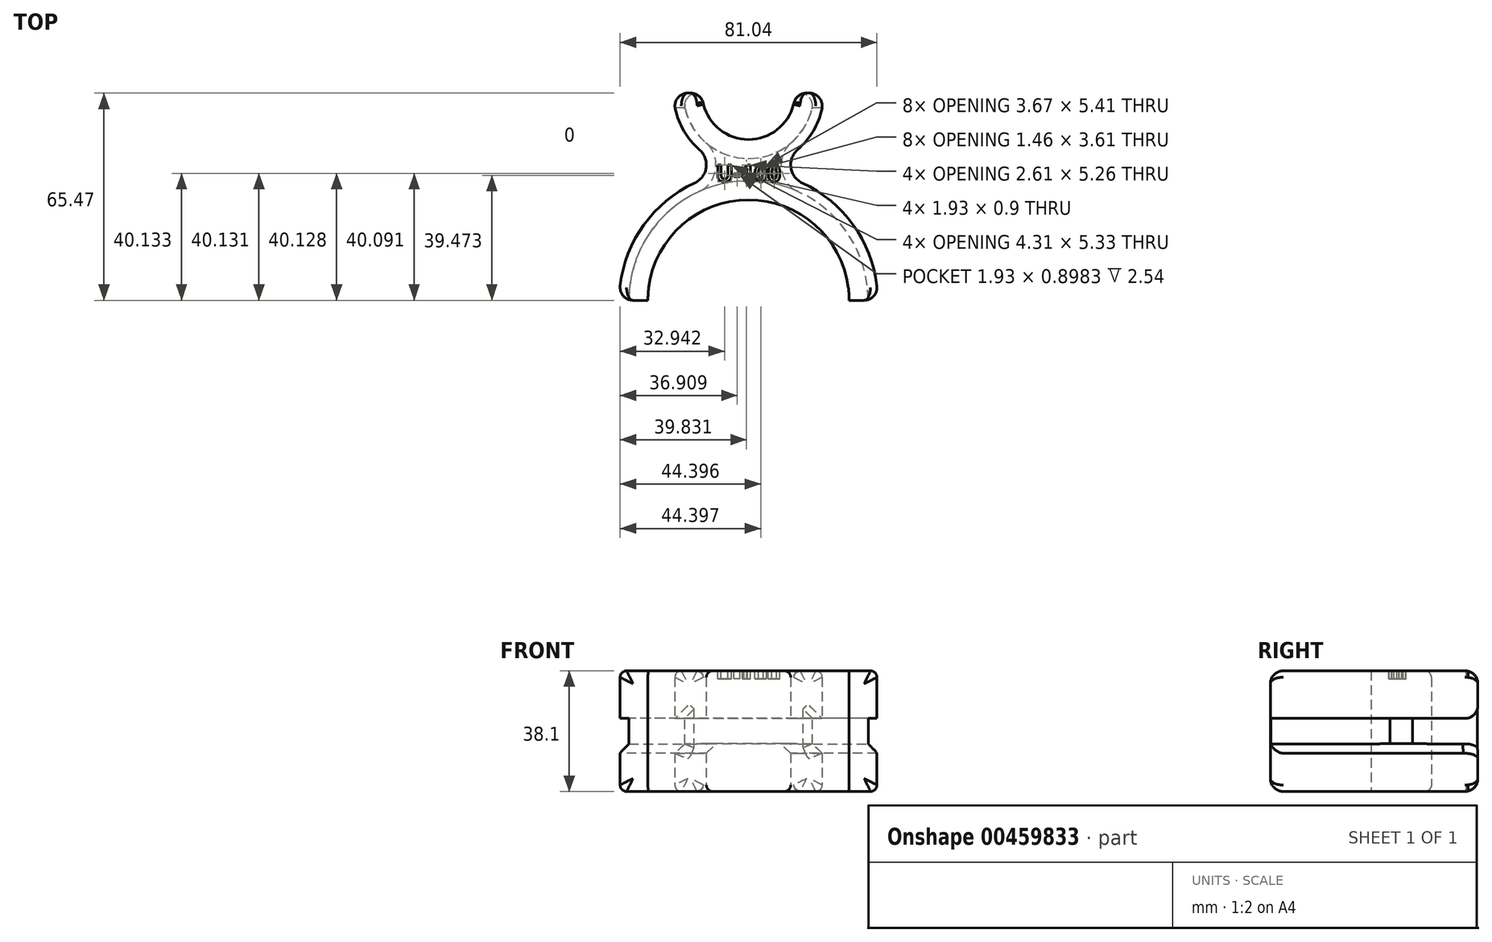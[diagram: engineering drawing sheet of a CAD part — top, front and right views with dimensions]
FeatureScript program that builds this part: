
annotation { "Feature Type Name" : "Feature", "Feature Type Description" : "" }
export const myFeature = defineFeature(function(context is Context, id is Id, definition is map)
    precondition{}
    {
        {
            var Q0;
            Q0=qCreatedBy(makeId("Top.planeOp"),FACE);
            var sketch = newSketch(context, id + "F0", { "sketchPlane" : qUnion([Q0])});
            skArc(sketch, "E0", {"start": v(31.75, -42.8) * mm, "mid": v(0, -11.05) * mm, "end": v(-31.75, -42.8) * mm});
            skLineSegment(sketch, "E1", {"start": v(31.75, -42.8) * mm, "end": v(40.75, -42.8) * mm});
            skArc(sketch, "E2", {"start": v(40.75, -42.8) * mm, "mid": v(34.3, -20.8) * mm, "end": v(17.02, -5.77) * mm});
            skArc(sketch, "E3", {"start": v(15.5, 4.8) * mm, "mid": v(21.53, 12.85) * mm, "end": v(23.66, 22.67) * mm});
            skArc(sketch, "E4", {"start": v(-17.02, -5.77) * mm, "mid": v(-34.3, -20.8) * mm, "end": v(-40.75, -42.8) * mm});
            skArc(sketch, "E5", {"start": v(-23.66, 22.67) * mm, "mid": v(-21.53, 12.85) * mm, "end": v(-15.5, 4.8) * mm});
            skLineSegment(sketch, "E6", {"start": v(-23.66, 22.67) * mm, "end": v(-14.66, 22.67) * mm});
            skLineSegment(sketch, "E7", {"start": v(23.66, 22.67) * mm, "end": v(14.66, 22.67) * mm});
            skLineSegment(sketch, "E8", {"start": v(-40.75, -42.8) * mm, "end": v(-31.75, -42.8) * mm});
            skArc(sketch, "E9", {"start": v(-14.66, 22.67) * mm, "mid": v(0, 8) * mm, "end": v(14.66, 22.67) * mm});
            skArc(sketch, "E10", {"start": v(-17.02, -5.77) * mm, "mid": v(-13.39, -0.9) * mm, "end": v(-15.5, 4.8) * mm});
            skArc(sketch, "E11", {"start": v(15.5, 4.8) * mm, "mid": v(13.39, -0.9) * mm, "end": v(17.02, -5.77) * mm});
            skLineSegment(sketch, "E12", {"start": v(-10.86, 8) * mm, "end": v(15, 8) * mm, "construction": true});
            skLineSegment(sketch, "E13", {"start": v(-10.28, -11.05) * mm, "end": v(13.06, -11.05) * mm, "construction": true});
            skArc(sketch, "E14", {"start": v(-20.66, 22.67) * mm, "mid": v(0, 2) * mm, "end": v(20.66, 22.67) * mm});
            skArc(sketch, "E15", {"start": v(37.75, -42.8) * mm, "mid": v(0, -5.05) * mm, "end": v(-37.75, -42.8) * mm});
            skCircle(sketch, "E16.cCircle", {"center": v(0, 22.67) * mm, "radius": 14.66 * mm, "construction": true});
            skLineSegment(sketch, "E16.0", {"start": v(-14.66, 22.67) * mm, "end": v(-7.33, 35.37) * mm, "construction": true});
            skLineSegment(sketch, "E16.1", {"start": v(-7.33, 35.37) * mm, "end": v(7.33, 35.37) * mm, "construction": true});
            skLineSegment(sketch, "E16.2", {"start": v(7.33, 35.37) * mm, "end": v(14.66, 22.67) * mm, "construction": true});
            skLineSegment(sketch, "E16.3", {"start": v(14.66, 22.67) * mm, "end": v(7.33, 9.97) * mm, "construction": true});
            skLineSegment(sketch, "E16.4", {"start": v(7.33, 9.97) * mm, "end": v(-7.33, 9.97) * mm, "construction": true});
            skLineSegment(sketch, "E16.5", {"start": v(-7.33, 9.97) * mm, "end": v(-14.66, 22.67) * mm, "construction": true});
            skSolve(sketch);
        }
        {
            var Q0;
            {var subQ0=sQuery(id+"F0.wireOp",EDGE,"E9");Q0=makeQuery(id+"F0.imprint","IMPRINT",FACE,{"disambiguationData":[TD([[makeQuery(id+"F0.imprint","IMPRINT",EDGE,{"derivedFrom":subQ0}),-1.0]])]});}
            var Q1;
            {var subQ0=sQuery(id+"F0.wireOp",EDGE,"E0");Q1=makeQuery(id+"F0.imprint","IMPRINT",FACE,{"disambiguationData":[TD([[makeQuery(id+"F0.imprint","IMPRINT",EDGE,{"derivedFrom":subQ0}),-1.0]])]});}
            var Q2;
            {var subQ8=sQuery(id+"F0.wireOp",EDGE,"E2");Q2=makeQuery(id+"F0.imprint","IMPRINT",FACE,{"disambiguationData":[TD([[makeQuery(id+"F0.imprint","IMPRINT",EDGE,{"derivedFrom":subQ8}),1.0]])]});}
            extrude(context, id + "F1", {"entities" : qUnion([Q0, Q1, Q2]), "endBound" : BoundingType.SYMMETRIC, "depth" : 38.1 * mm, "hasSecondDirection" : true, "secondDirectionOppositeDirection" : true, "secondDirectionDepth" : 20 * mm});
        }
        {
            var Q0;
            {var subQ8=sQuery(id+"F0.wireOp",EDGE,"E2");Q0=makeQuery(id+"F0.imprint","IMPRINT",FACE,{"disambiguationData":[TD([[makeQuery(id+"F0.imprint","IMPRINT",EDGE,{"derivedFrom":subQ8}),1.0]])]});}
            extrude(context, id + "F2", {"entities" : qUnion([Q0]), "operationType" : NewBodyOperationType.REMOVE, "endBound" : BoundingType.SYMMETRIC, "oppositeDirection" : true, "depth" : 8 * mm});
        }
        {
            var Q0;
            Q0=makeQuery(id+"F2.boolean.opBoolean","COPY",EDGE,{"derivedFrom":makeQuery(id+"F2.opExtrude","CAP_EDGE",EDGE,{"disambiguationData":[OSD([sQuery(id+"F0.wireOp",EDGE,"E2")])],"isStart":true})});
            var Q1;
            Q1=makeQuery(id+"F2.boolean.opBoolean","COPY",EDGE,{"derivedFrom":makeQuery(id+"F2.opExtrude","CAP_EDGE",EDGE,{"disambiguationData":[OSD([sQuery(id+"F0.wireOp",EDGE,"E2")])],"isStart":false})});
            var Q2;
            Q2=makeQuery(id+"F2.boolean.opBoolean","COPY",EDGE,{"derivedFrom":makeQuery(id+"F2.opExtrude","CAP_EDGE",EDGE,{"disambiguationData":[OSD([sQuery(id+"F0.wireOp",EDGE,"E4")])],"isStart":true})});
            var Q3;
            Q3=makeQuery(id+"F2.boolean.opBoolean","COPY",EDGE,{"derivedFrom":makeQuery(id+"F2.opExtrude","CAP_EDGE",EDGE,{"disambiguationData":[OSD([sQuery(id+"F0.wireOp",EDGE,"E4")])],"isStart":false})});
            chamfer(context, id + "F3", {"entities" : qUnion([Q0, Q1, Q2, Q3]), "width" : 3.05 * mm, "tangentPropagation" : true});
        }
        {
            var Q0;
            Q0=makeQuery(id+"F1.opExtrude","CAP_EDGE",EDGE,{"disambiguationData":[OSD([sQuery(id+"F0.wireOp",EDGE,"E9")])],"isStart":false});
            var Q1;
            Q1=makeQuery(id+"F1.opExtrude","CAP_EDGE",EDGE,{"disambiguationData":[OSD([sQuery(id+"F0.wireOp",EDGE,"E5")])],"isStart":false});
            var Q2;
            Q2=makeQuery(id+"F1.opExtrude","CAP_EDGE",EDGE,{"disambiguationData":[OSD([sQuery(id+"F0.wireOp",EDGE,"E3")])],"isStart":false});
            var Q3;
            Q3=makeQuery(id+"F1.opExtrude","CAP_EDGE",EDGE,{"disambiguationData":[OSD([sQuery(id+"F0.wireOp",EDGE,"E9")])],"isStart":true});
            var Q4;
            Q4=makeQuery(id+"F1.opExtrude","CAP_EDGE",EDGE,{"disambiguationData":[OSD([sQuery(id+"F0.wireOp",EDGE,"E3")])],"isStart":true});
            var Q5;
            Q5=makeQuery(id+"F1.opExtrude","CAP_EDGE",EDGE,{"disambiguationData":[OSD([sQuery(id+"F0.wireOp",EDGE,"E5")])],"isStart":true});
            fillet(context, id + "F4", {"entities" : qUnion([Q0, Q1, Q2, Q3, Q4, Q5]), "radius" : 2.03 * mm, "tangentPropagation" : true, "allowEdgeOverflow" : false});
        }
        {
            var Q0;
            Q0=makeQuery(id+"F1.opExtrude","SWEPT_FACE",FACE,{"disambiguationData":[OSD([sQuery(id+"F0.wireOp",EDGE,"E7")])]});
            var Q1;
            Q1=makeQuery(id+"F1.opExtrude","SWEPT_FACE",FACE,{"disambiguationData":[OSD([sQuery(id+"F0.wireOp",EDGE,"E6")])]});
            var Q2;
            {var subQ0=sQuery(id+"F0.wireOp",EDGE,"E11");var subQ1=sQuery(id+"F0.wireOp",EDGE,"E10");var subQ2=sQuery(id+"F0.wireOp",EDGE,"E8");var subQ3=sQuery(id+"F0.wireOp",EDGE,"E7");var subQ4=sQuery(id+"F0.wireOp",EDGE,"E6");var subQ5=sQuery(id+"F0.wireOp",EDGE,"E5");var subQ6=sQuery(id+"F0.wireOp",EDGE,"E4");var subQ7=sQuery(id+"F0.wireOp",EDGE,"E3");var subQ8=sQuery(id+"F0.wireOp",EDGE,"E2");var subQ9=sQuery(id+"F0.wireOp",EDGE,"E1");Q2=makeQuery(id+"F2.boolean.opBoolean","SPLIT",EDGE,{"disambiguationData":[TD([makeQuery(id+"F1.opExtrude","CAP_FACE",FACE,{"disambiguationData":[OSD([sQuery(id+"F0.wireOp",EDGE,"E0"),subQ9,subQ8,subQ7,subQ6,subQ5,subQ4,subQ3,subQ2,sQuery(id+"F0.wireOp",EDGE,"E9"),subQ1,subQ0])],"isStart":false})])],"derivedFrom":makeQuery(id+"F1.opExtrude","SWEPT_EDGE",EDGE,{"disambiguationData":[OSD([subQ9,subQ8])]})});}
            var Q3;
            {var subQ0=sQuery(id+"F0.wireOp",EDGE,"E11");var subQ1=sQuery(id+"F0.wireOp",EDGE,"E10");var subQ2=sQuery(id+"F0.wireOp",EDGE,"E8");var subQ3=sQuery(id+"F0.wireOp",EDGE,"E7");var subQ4=sQuery(id+"F0.wireOp",EDGE,"E6");var subQ5=sQuery(id+"F0.wireOp",EDGE,"E5");var subQ6=sQuery(id+"F0.wireOp",EDGE,"E4");var subQ7=sQuery(id+"F0.wireOp",EDGE,"E3");var subQ8=sQuery(id+"F0.wireOp",EDGE,"E2");var subQ9=sQuery(id+"F0.wireOp",EDGE,"E1");Q3=makeQuery(id+"F2.boolean.opBoolean","SPLIT",EDGE,{"disambiguationData":[TD([makeQuery(id+"F1.opExtrude","CAP_FACE",FACE,{"disambiguationData":[OSD([sQuery(id+"F0.wireOp",EDGE,"E0"),subQ9,subQ8,subQ7,subQ6,subQ5,subQ4,subQ3,subQ2,sQuery(id+"F0.wireOp",EDGE,"E9"),subQ1,subQ0])],"isStart":false})])],"derivedFrom":makeQuery(id+"F1.opExtrude","SWEPT_EDGE",EDGE,{"disambiguationData":[OSD([subQ6,subQ2])]})});}
            var Q4;
            {var subQ0=sQuery(id+"F0.wireOp",EDGE,"E11");var subQ1=sQuery(id+"F0.wireOp",EDGE,"E10");var subQ2=sQuery(id+"F0.wireOp",EDGE,"E8");var subQ3=sQuery(id+"F0.wireOp",EDGE,"E7");var subQ4=sQuery(id+"F0.wireOp",EDGE,"E6");var subQ5=sQuery(id+"F0.wireOp",EDGE,"E5");var subQ6=sQuery(id+"F0.wireOp",EDGE,"E4");var subQ7=sQuery(id+"F0.wireOp",EDGE,"E3");var subQ8=sQuery(id+"F0.wireOp",EDGE,"E2");var subQ9=sQuery(id+"F0.wireOp",EDGE,"E1");Q4=makeQuery(id+"F2.boolean.opBoolean","SPLIT",EDGE,{"disambiguationData":[TD([makeQuery(id+"F1.opExtrude","CAP_FACE",FACE,{"disambiguationData":[OSD([sQuery(id+"F0.wireOp",EDGE,"E0"),subQ9,subQ8,subQ7,subQ6,subQ5,subQ4,subQ3,subQ2,sQuery(id+"F0.wireOp",EDGE,"E9"),subQ1,subQ0])],"isStart":true})])],"derivedFrom":makeQuery(id+"F1.opExtrude","SWEPT_EDGE",EDGE,{"disambiguationData":[OSD([subQ6,subQ2])]})});}
            var Q5;
            {var subQ0=sQuery(id+"F0.wireOp",EDGE,"E11");var subQ1=sQuery(id+"F0.wireOp",EDGE,"E10");var subQ2=sQuery(id+"F0.wireOp",EDGE,"E8");var subQ3=sQuery(id+"F0.wireOp",EDGE,"E7");var subQ4=sQuery(id+"F0.wireOp",EDGE,"E6");var subQ5=sQuery(id+"F0.wireOp",EDGE,"E5");var subQ6=sQuery(id+"F0.wireOp",EDGE,"E4");var subQ7=sQuery(id+"F0.wireOp",EDGE,"E3");var subQ8=sQuery(id+"F0.wireOp",EDGE,"E2");var subQ9=sQuery(id+"F0.wireOp",EDGE,"E1");Q5=makeQuery(id+"F2.boolean.opBoolean","SPLIT",EDGE,{"disambiguationData":[TD([makeQuery(id+"F1.opExtrude","CAP_FACE",FACE,{"disambiguationData":[OSD([sQuery(id+"F0.wireOp",EDGE,"E0"),subQ9,subQ8,subQ7,subQ6,subQ5,subQ4,subQ3,subQ2,sQuery(id+"F0.wireOp",EDGE,"E9"),subQ1,subQ0])],"isStart":true})])],"derivedFrom":makeQuery(id+"F1.opExtrude","SWEPT_EDGE",EDGE,{"disambiguationData":[OSD([subQ9,subQ8])]})});}
            fillet(context, id + "F5", {"entities" : qUnion([Q0, Q1, Q2, Q3, Q4, Q5]), "radius" : 4.06 * mm, "tangentPropagation" : true, "allowEdgeOverflow" : false});
        }
        {
            var Q0;
            Q0=makeQuery(id+"F1.opExtrude","CAP_FACE",FACE,{"disambiguationData":[OSD([sQuery(id+"F0.wireOp",EDGE,"E0"),sQuery(id+"F0.wireOp",EDGE,"E1"),sQuery(id+"F0.wireOp",EDGE,"E2"),sQuery(id+"F0.wireOp",EDGE,"E3"),sQuery(id+"F0.wireOp",EDGE,"E4"),sQuery(id+"F0.wireOp",EDGE,"E5"),sQuery(id+"F0.wireOp",EDGE,"E6"),sQuery(id+"F0.wireOp",EDGE,"E7"),sQuery(id+"F0.wireOp",EDGE,"E8"),sQuery(id+"F0.wireOp",EDGE,"E9"),sQuery(id+"F0.wireOp",EDGE,"E10"),sQuery(id+"F0.wireOp",EDGE,"E11")])],"isStart":false});
            var sketch = newSketch(context, id + "F6", { "sketchPlane" : qUnion([Q0])});
            skText(sketch, "E17", { "text": "U-100", "fontName": "OpenSans-Bold.ttf"});
            const initialGuessF6  = {"E17": [-0.01036, -0.0053, 1, 0, 0.0053]};
            skSetInitialGuess(sketch, initialGuessF6);
            skSolve(sketch);
        }
        {
            var Q0;
            Q0=qSketchRegion(id+"F6",true);
            extrude(context, id + "F7", {"entities" : qUnion([Q0]), "operationType" : NewBodyOperationType.REMOVE, "oppositeDirection" : true, "depth" : 2.54 * mm});
        }
    });
